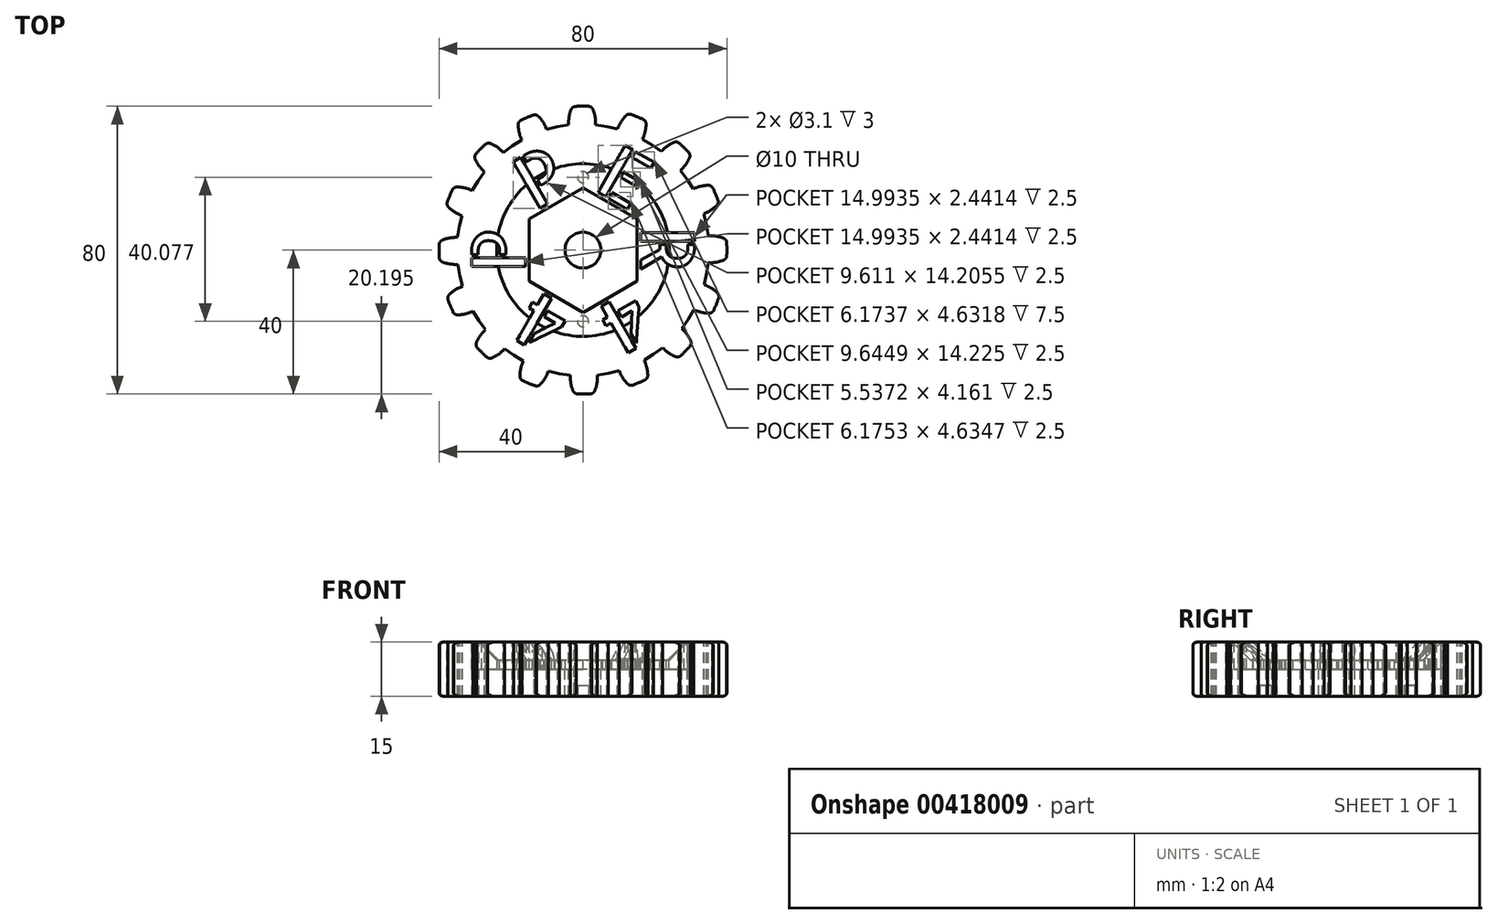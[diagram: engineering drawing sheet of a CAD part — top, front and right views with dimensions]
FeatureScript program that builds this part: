
annotation { "Feature Type Name" : "Feature", "Feature Type Description" : "" }
export const myFeature = defineFeature(function(context is Context, id is Id, definition is map)
    precondition{}
    {
        {
            assignVariable(context, id + "F0", {"name" : "epaisseur_jeton", "anyValue" : 10});
        }
        {
            assignVariable(context, id + "F1", {"name" : "profondeur_lettre", "anyValue" : (getVariable(context, 'epaisseur_jeton') * 1.5) / 2});
        }
        {
            var Q0;
            Q0=qCreatedBy(makeId("Front.planeOp"),FACE);
            var sketch = newSketch(context, id + "F2", { "sketchPlane" : qUnion([Q0])});
            skLineSegment(sketch, "E0.top", {"start": v(0, 10) * mm, "end": v(-24, 10) * mm});
            skLineSegment(sketch, "E0.left", {"start": v(0, 0) * mm, "end": v(0, 10) * mm});
            skLineSegment(sketch, "E1.top", {"start": v(-24, 15) * mm, "end": v(-40, 15) * mm});
            skLineSegment(sketch, "E1.left", {"start": v(-24, 10) * mm, "end": v(-24, 15) * mm});
            skLineSegment(sketch, "E1.right", {"start": v(-40, 0) * mm, "end": v(-40, 15) * mm});
            skLineSegment(sketch, "E2", {"start": v(-40, 0) * mm, "end": v(0, 0) * mm});
            skSolve(sketch);
        }
        {
            var Q0;
            Q0=makeQuery(id+"F2.imprint","IMPRINT",FACE,{"disambiguationData":[TD([[makeQuery(id+"F2.imprint","IMPRINT",EDGE,{"derivedFrom":sQuery(id+"F2.wireOp",EDGE,"E0.top")}),1.0]])]});
            var Q1;
            Q1=sQuery(id+"F2.wireOp",EDGE,"E0.left");
            revolve(context, id + "F3", {"entities" : qUnion([Q0]), "axis" : qUnion([Q1]), "revolveType" : RevolveType.FULL});
        }
        {
            var Q0;
            Q0=makeQuery(id+"F3.opRevolve","SWEPT_EDGE",EDGE,{"disambiguationData":[OSD([sQuery(id+"F2.wireOp",EDGE,"E1.top"),sQuery(id+"F2.wireOp",EDGE,"E1.left")])]});
            chamfer(context, id + "F4", {"entities" : qUnion([Q0]), "width" : 5 * mm, "tangentPropagation" : true});
        }
        {
            var Q0;
            {var subQ0=sQuery(id+"F2.wireOp",EDGE,"E1.top");Q0=makeQuery(id+"F4.opChamfer","BLEND_EDGE",EDGE,{"blendedFrom":[makeQuery(id+"F3.opRevolve","SWEPT_EDGE",EDGE,{"disambiguationData":[OSD([subQ0,sQuery(id+"F2.wireOp",EDGE,"E1.left")])]}),makeQuery(id+"F3.opRevolve","SWEPT_FACE",FACE,{"disambiguationData":[OSD([subQ0])]})],"blendedInto":[makeQuery(id+"F3.opRevolve","SWEPT_FACE",FACE,{"disambiguationData":[OSD([subQ0])]})]});}
            var Q1;
            Q1=makeQuery(id+"F3.opRevolve","SWEPT_EDGE",EDGE,{"disambiguationData":[OSD([sQuery(id+"F2.wireOp",EDGE,"E1.top"),sQuery(id+"F2.wireOp",EDGE,"E1.right")])]});
            var Q2;
            Q2=makeQuery(id+"F3.opRevolve","SWEPT_EDGE",EDGE,{"disambiguationData":[OSD([sQuery(id+"F2.wireOp",EDGE,"E1.right"),sQuery(id+"F2.wireOp",EDGE,"E2")])]});
            fillet(context, id + "F5", {"entities" : qUnion([Q0, Q1, Q2]), "radius" : 1 * mm, "tangentPropagation" : true, "allowEdgeOverflow" : false});
        }
        {
            var Q0;
            Q0=makeQuery(id+"F3.opRevolve","SWEPT_FACE",FACE,{"disambiguationData":[OSD([sQuery(id+"F2.wireOp",EDGE,"E1.top")])]});
            var sketch = newSketch(context, id + "F6", { "sketchPlane" : qUnion([Q0])});
            skCircle(sketch, "E3.cCircle", {"center": v(0, 0) * mm, "radius": 15 * mm, "construction": true});
            skLineSegment(sketch, "E3.0", {"start": v(-15, 8.66) * mm, "end": v(0, 17.32) * mm});
            skLineSegment(sketch, "E3.1", {"start": v(0, 17.32) * mm, "end": v(15, 8.66) * mm});
            skLineSegment(sketch, "E3.2", {"start": v(15, 8.66) * mm, "end": v(15, -8.66) * mm});
            skLineSegment(sketch, "E3.3", {"start": v(15, -8.66) * mm, "end": v(0, -17.32) * mm});
            skLineSegment(sketch, "E3.4", {"start": v(0, -17.32) * mm, "end": v(-15, -8.66) * mm});
            skLineSegment(sketch, "E3.5", {"start": v(-15, -8.66) * mm, "end": v(-15, 8.66) * mm});
            skPoint(sketch, "E3.0.midPoint", {"position": v(-7.5, 13) * mm});
            skText(sketch, "E4", { "text": "P", "fontName": "AllertaStencil-Regular.ttf"});
            skText(sketch, "E5", { "text": "P", "fontName": "AllertaStencil-Regular.ttf"});
            skText(sketch, "E6", { "text": "E", "fontName": "AllertaStencil-Regular.ttf"});
            skText(sketch, "E7", { "text": "4", "fontName": "AllertaStencil-Regular.ttf"});
            skText(sketch, "E8", { "text": "R", "fontName": "AllertaStencil-Regular.ttf"});
            skText(sketch, "E9", { "text": "4", "fontName": "AllertaStencil-Regular.ttf"});
            skLineSegment(sketch, "E10", {"start": v(0, 0) * mm, "end": v(7.5, -13) * mm, "construction": true});
            skLineSegment(sketch, "E11", {"start": v(0, 0) * mm, "end": v(15, 0) * mm, "construction": true});
            skLineSegment(sketch, "E12", {"start": v(0, 0) * mm, "end": v(-7.5, 13) * mm, "construction": true});
            skLineSegment(sketch, "E13", {"start": v(0, 0) * mm, "end": v(-15, 0) * mm, "construction": true});
            skLineSegment(sketch, "E14", {"start": v(0, 0) * mm, "end": v(-7.5, -13) * mm, "construction": true});
            skLineSegment(sketch, "E15", {"start": v(0, 0) * mm, "end": v(7.5, 13) * mm, "construction": true});
            skCircle(sketch, "E16", {"center": v(0, 0) * mm, "radius": 5 * mm});
            const initialGuessF6  = {"E4": [-0.016, -0.0064, 0, 1, 0.015], "E5": [-0.01354, 0.01066, 0.86603, 0.5, 0.015], "E6": [0.0025, 0.01703, 0.86603, -0.5, 0.015], "E7": [-0.0025, -0.01703, -0.86603, 0.5, 0.015], "E8": [0.016, 0.0067, 0, -1, 0.015], "E9": [0.0135, -0.01068, -0.86603, -0.5, 0.015]};
            skSetInitialGuess(sketch, initialGuessF6);
            skSolve(sketch);
        }
        {
            var Q0;
            Q0 = qSketchRegion(id + "F6", true);
            extrude(context, id + "F7", {"entities" : qUnion([Q0]), "operationType" : NewBodyOperationType.REMOVE, "oppositeDirection" : true, "depth" : (getVariable(context, 'profondeur_lettre')) * mm});
        }
        {
            var Q0;
            Q0=makeQuery(id+"F3.opRevolve","SWEPT_FACE",FACE,{"disambiguationData":[OSD([sQuery(id+"F2.wireOp",EDGE,"E1.top")])]});
            var sketch = newSketch(context, id + "F8", { "sketchPlane" : qUnion([Q0])});
            skLineSegment(sketch, "E17", {"start": v(0, 0) * mm, "end": v(0, 58.2) * mm, "construction": true});
            skCircle(sketch, "E18", {"center": v(0, 0) * mm, "radius": 35 * mm, "construction": true});
            skCircle(sketch, "E19", {"center": v(0, 0) * mm, "radius": 37.5 * mm, "construction": true});
            skLineSegment(sketch, "E20", {"start": v(-4, 34.77) * mm, "end": v(-4, 35.43) * mm});
            skLineSegment(sketch, "E21", {"start": v(0, 40) * mm, "end": v(0, 35) * mm});
            skLineSegment(sketch, "E22", {"start": v(-4, 34.77) * mm, "end": v(-7.06, 34.28) * mm});
            skLineSegment(sketch, "E23", {"start": v(0, 0) * mm, "end": v(-4, 34.77) * mm, "construction": true});
            skLineSegment(sketch, "E24", {"start": v(-4, 34.77) * mm, "end": v(-5, 43.52) * mm, "construction": true});
            skLineSegment(sketch, "E25", {"start": v(-7.06, 34.28) * mm, "end": v(-8.49, 41.21) * mm, "construction": true});
            skLineSegment(sketch, "E26.MirrorCS", {"start": v(-10.07, 33.52) * mm, "end": v(-7.06, 34.28) * mm});
            skLineSegment(sketch, "E27", {"start": v(0, 0) * mm, "end": v(-7.07, 34.3) * mm, "construction": true});
            skCircle(sketch, "E28", {"center": v(0, 0) * mm, "radius": 39 * mm, "construction": true});
            skPoint(sketch, "E29.visualSharp", {"position": v(-4, 37.29) * mm});
            skArc(sketch, "E29.filletArc", {"start": v(-3.33, 39.02) * mm, "mid": v(-3.83, 37.25) * mm, "end": v(-4, 35.43) * mm});
            skLineSegment(sketch, "E30", {"start": v(-2.47, 39.88) * mm, "end": v(-1.31, 40.43) * mm});
            skLineSegment(sketch, "E31", {"start": v(-1.31, 40.43) * mm, "end": v(-8.49, 41.21) * mm});
            skArc(sketch, "E32", {"start": v(-3.33, 39.02) * mm, "mid": v(-3, 39.54) * mm, "end": v(-2.47, 39.88) * mm});
            skLineSegment(sketch, "E33.MirrorCS", {"start": v(-14.77, 37.65) * mm, "end": v(-8.49, 41.21) * mm});
            skLineSegment(sketch, "E34.MirrorCS", {"start": v(-13.5, 37.6) * mm, "end": v(-14.77, 37.65) * mm});
            skArc(sketch, "E35.MirrorCS", {"start": v(-12.36, 37.16) * mm, "mid": v(-12.88, 37.5) * mm, "end": v(-13.5, 37.6) * mm});
            skArc(sketch, "E36.MirrorCS", {"start": v(-12.36, 37.16) * mm, "mid": v(-11.2, 35.74) * mm, "end": v(-10.33, 34.13) * mm});
            skLineSegment(sketch, "E37.MirrorCS", {"start": v(-10.07, 33.52) * mm, "end": v(-10.33, 34.13) * mm});
            skSolve(sketch);
        }
        {
            var Q0;
            Q0=makeQuery(id+"F8.imprint","IMPRINT",FACE,{"disambiguationData":[TD([[makeQuery(id+"F8.imprint","IMPRINT",EDGE,{"derivedFrom":sQuery(id+"F8.wireOp",EDGE,"E20")}),1.0]])]});
            var Q1;
            Q1=makeQuery(id+"F8.imprint","IMPRINT",FACE,{"disambiguationData":[TD([[makeQuery(id+"F8.imprint","IMPRINT",EDGE,{"derivedFrom":sQuery(id+"F8.wireOp",EDGE,"E30")}),1.0]])]});
            extrude(context, id + "F9", {"entities" : qUnion([Q0, Q1]), "oppositeDirection" : true, "depth" : 25 * mm, "hasSecondDirection" : true, "secondDirectionOppositeDirection" : false, "secondDirectionDepth" : 19 * mm});
        }
        {
            var Q0;
            Q0=makeQuery(id+"F9.opExtrude","SWEPT_BODY",BODY,{"disambiguationData":[OSD([sQuery(id+"F8.wireOp",EDGE,"E20"),sQuery(id+"F8.wireOp",EDGE,"oqj8jshl-01il-bNOT-rA4I-LJmCCW0eeGWJ"),sQuery(id+"F8.wireOp",EDGE,"E22"),sQuery(id+"F8.wireOp",EDGE,"34faa27b-707b-4d5b-a58c-ec610780bd600.MirrorCS"),sQuery(id+"F8.wireOp",EDGE,"4e9da0ac-927a-4e3b-8406-2053cba918760.MirrorCS"),sQuery(id+"F8.wireOp",EDGE,"E26.MirrorCS"),sQuery(id+"F8.wireOp",EDGE,"fkDhdseK-Lo3c-hOCe-335R-vuvbFg0r0E3J"),sQuery(id+"F8.wireOp",EDGE,"b1e6bd13-f833-4745-9b72-8ad42e935bc90.MirrorCS")])]});
            var Q1;
            Q1=sQuery(id+"F2.wireOp",EDGE,"E0.left");
            circularPattern(context, id + "F10", {"operationType" : NewBodyOperationType.REMOVE, "entities" : qUnion([Q0]), "axis" : qUnion([Q1]), "angle" : 360 * degree, "instanceCount" : 16, "equalSpace" : true, "isCentered" : true});
        }
        {
            var Q0;
            Q0=makeQuery(id+"F7.boolean.opBoolean","SPLIT",FACE,{"disambiguationData":[TD([makeQuery(id+"F7.opExtrude","SWEPT_FACE",FACE,{"disambiguationData":[OSD([sQuery(id+"F6.wireOp",EDGE,"E16")])]})])],"derivedFrom":makeQuery(id+"F3.opRevolve","SWEPT_FACE",FACE,{"disambiguationData":[OSD([sQuery(id+"F2.wireOp",EDGE,"E0.top")])]})});
            var Q1;
            Q1=makeQuery(id+"F3.opRevolve","SWEPT_FACE",FACE,{"disambiguationData":[OSD([sQuery(id+"F2.wireOp",EDGE,"E2")])]});
            extrude(context, id + "F11", {"entities" : qUnion([Q0]), "operationType" : NewBodyOperationType.REMOVE, "endBound" : BoundingType.UP_TO_SURFACE, "oppositeDirection" : true, "endBoundEntityFace" : qUnion([Q1]), "depth" : 25 * mm});
        }
        {
            var Q0;
            Q0=makeQuery(id+"F3.opRevolve","SWEPT_FACE",FACE,{"disambiguationData":[OSD([sQuery(id+"F2.wireOp",EDGE,"E2")])]});
            var sketch = newSketch(context, id + "F12", { "sketchPlane" : qUnion([Q0])});
            skCircle(sketch, "E38", {"center": v(0, -20.27) * mm, "radius": 1.55 * mm});
            skCircle(sketch, "E39", {"center": v(0, 19.8) * mm, "radius": 1.55 * mm});
            skSolve(sketch);
        }
        {
            var Q0;
            Q0=makeQuery(id+"F12.imprint","IMPRINT",FACE,{"disambiguationData":[TD([[makeQuery(id+"F12.imprint","IMPRINT",EDGE,{"derivedFrom":sQuery(id+"F12.wireOp",EDGE,"E38")}),1.0]])]});
            var Q1;
            Q1=makeQuery(id+"F12.imprint","IMPRINT",FACE,{"disambiguationData":[TD([[makeQuery(id+"F12.imprint","IMPRINT",EDGE,{"derivedFrom":sQuery(id+"F12.wireOp",EDGE,"E39")}),1.0]])]});
            extrude(context, id + "F13", {"entities" : qUnion([Q0, Q1]), "operationType" : NewBodyOperationType.REMOVE, "oppositeDirection" : true, "depth" : 3 * mm, "offsetDistance" : 25 * mm});
        }
    });
